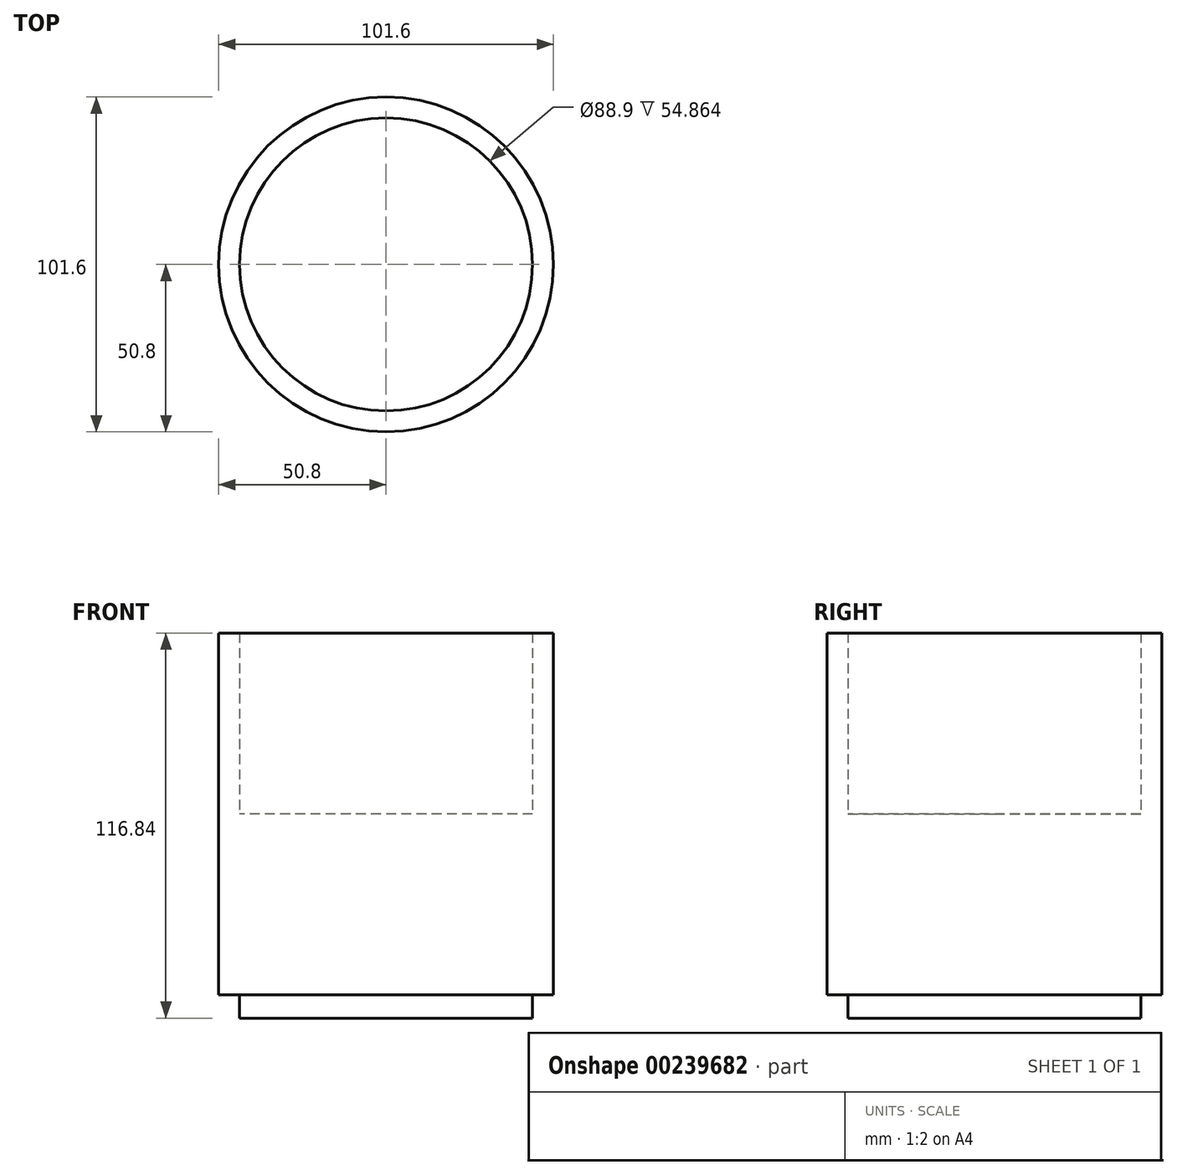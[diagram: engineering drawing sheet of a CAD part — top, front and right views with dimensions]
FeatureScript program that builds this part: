
annotation { "Feature Type Name" : "Feature", "Feature Type Description" : "" }
export const myFeature = defineFeature(function(context is Context, id is Id, definition is map)
    precondition{}
    {
        {
            var Q0;
            Q0=qCreatedBy(makeId("Top.planeOp"),FACE);
            var sketch = newSketch(context, id + "F0", { "sketchPlane" : qUnion([Q0])});
            skCircle(sketch, "E0", {"center": v(0, 0) * mm, "radius": 50.8 * mm});
            skCircle(sketch, "E1", {"center": v(0, 0) * mm, "radius": 44.45 * mm});
            skSolve(sketch);
        }
        {
            var Q0;
            Q0 = qSketchRegion(id + "F0", true);
            extrude(context, id + "F1", {"entities" : qUnion([Q0]), "endBound" : BoundingType.SYMMETRIC, "depth" : 109.73 * mm});
        }
        {
            var Q0;
            Q0=qCreatedBy(makeId("Front.planeOp"),FACE);
            var sketch = newSketch(context, id + "F2", { "sketchPlane" : qUnion([Q0])});
            skArc(sketch, "E2", {"start": v(51.13, -40.94) * mm, "mid": v(76.22, 0.13) * mm, "end": v(50.72, 40.94) * mm});
            skArc(sketch, "E3", {"start": v(50.87, -34.53) * mm, "mid": v(68.83, 0.05) * mm, "end": v(50.66, 34.53) * mm});
            skSolve(sketch);
        }
        {
            var Q0;
            Q0=makeQuery(id+"F0.imprint","IMPRINT",FACE,{"disambiguationData":[TD([[makeQuery(id+"F0.imprint","IMPRINT",EDGE,{"derivedFrom":sQuery(id+"F0.wireOp",EDGE,"E1")}),1.0]])]});
            extrude(context, id + "F3", {"entities" : qUnion([Q0]), "operationType" : NewBodyOperationType.ADD, "oppositeDirection" : true, "depth" : 61.98 * mm});
        }
        {
            var Q0;
            Q0=sQuery(id+"F2.wireOp",EDGE,"E2");
            var Q1;
            Q1=sQuery(id+"F2.wireOp",EDGE,"E3");
            extrude(context, id + "F4", {"bodyType" : ToolBodyType.SURFACE, "surfaceEntities" : qUnion([Q0, Q1]), "depth" : 9.9 * mm});
        }
    });
